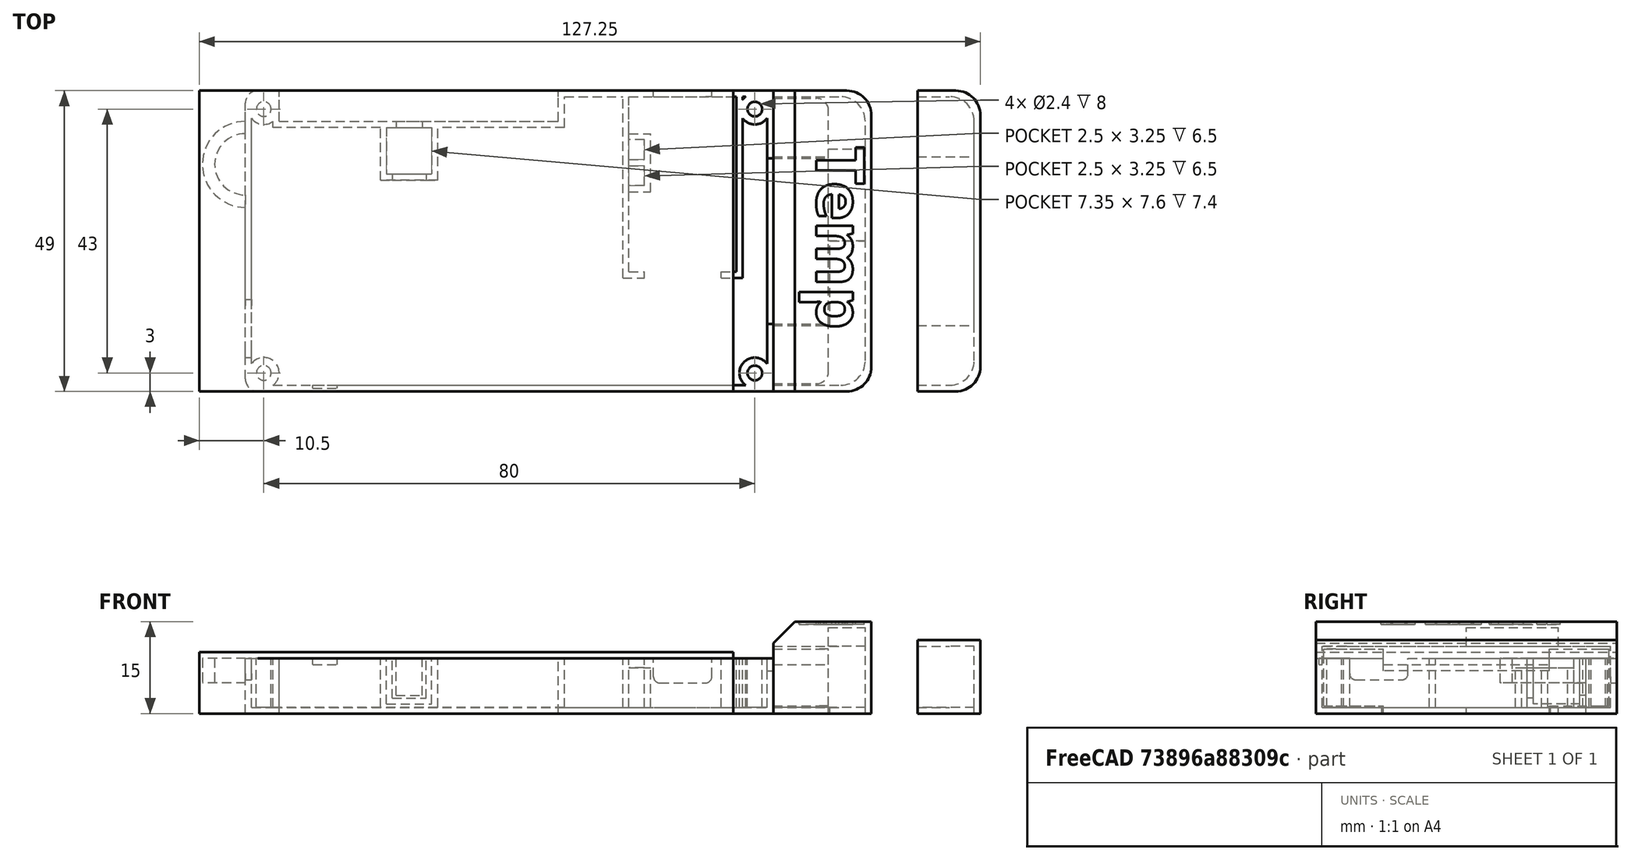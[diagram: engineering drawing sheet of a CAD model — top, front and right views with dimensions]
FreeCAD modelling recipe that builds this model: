
FCSTD DOCUMENT  (FreeCAD 0.20R29410 (Git))
Label: badger2040_case
License: All rights reserved
LicenseURL: http://en.wikipedia.org/wiki/All_rights_reserved
objects: Part::Box×30, Part::MultiFuse×11, Part::Cylinder×10, Part::Cut×10, Part::Fillet×9, Part::Part2DObjectPython×1, Part::Extrusion×1, Part::Chamfer×1
note: 73 computed .brp shape members not serialized (recipe doc carries the construction recipe); baked Part::Feature solids carry a one-line shape summary decoded from their .brp

FEATURE [Part::Box] Box  label="Cube(outer)"
  AttacherType = Attacher::AttachEngine3D
  Height = 9
  Length = 86
  Placement = pos=(0.5,0,-1) rot=(0,0,1;0rad)
  Width = 49
FEATURE [Part::Box] Box001  label="Cube001(connector_cutter)"
  AttacherType = Attacher::AttachEngine3D
  Height = 2
  Length = 10
  Placement = pos=(85.5,11,6) rot=(0,0,1;0rad)
  Width = 27
FEATURE [Part::Cylinder] Cylinder  label="Cylinder(top_left_thread)"
  Angle = 360
  AttacherType = Attacher::AttachEngine3D
  FirstAngle = 0
  Height = 10
  Placement = pos=(3.5,3,0) rot=(0,0,1;0rad)
  Radius = 1.2
  SecondAngle = 0
FEATURE [Part::Cylinder] Cylinder001  label="Cylinder001(top_right_thread)"
  Angle = 360
  AttacherType = Attacher::AttachEngine3D
  FirstAngle = 0
  Height = 10
  Placement = pos=(83.5,3,0) rot=(0,0,1;0rad)
  Radius = 1.2
  SecondAngle = 0
FEATURE [Part::Cylinder] Cylinder002  label="Cylinder002(bottom_left_thread)"
  Angle = 360
  AttacherType = Attacher::AttachEngine3D
  FirstAngle = 0
  Height = 10
  Placement = pos=(3.5,46,0) rot=(0,0,1;0rad)
  Radius = 1.2
  SecondAngle = 0
FEATURE [Part::Cylinder] Cylinder003  label="Cylinder003(bottom_right_thread)"
  Angle = 360
  AttacherType = Attacher::AttachEngine3D
  FirstAngle = 0
  Height = 10
  Placement = pos=(83.5,46,0) rot=(0,0,1;0rad)
  Radius = 1.2
  SecondAngle = 0
FEATURE [Part::Box] Box002  label="Cube(usb_c_charging)"
  AttacherType = Attacher::AttachEngine3D
  Height = 4
  Length = 9.5
  Placement = pos=(67,48,4) rot=(0,0,1;0rad)
  Width = 1
FEATURE [Part::Box] Box003  label="Cube(inner"
  AttacherType = Attacher::AttachEngine3D
  Height = 8
  Length = 84
  Placement = pos=(1.5,1,0) rot=(0,0,1;0rad)
  Width = 47
FEATURE [Part::Box] Box004  label="Cube(button_cutter)"
  AttacherType = Attacher::AttachEngine3D
  Height = 9
  Length = 45.5
  Placement = pos=(6,44,-1) rot=(0,0,1;0rad)
  Width = 5
FEATURE [Part::Box] Box005  label="Cube(button_cutter_wall)"
  AttacherType = Attacher::AttachEngine3D
  Height = 9
  Length = 47.5
  Placement = pos=(5,43,-1) rot=(0,0,1;0rad)
  Width = 6
FEATURE [Part::Box] Box006  label="Cube(usb_c_upload)"
  AttacherType = Attacher::AttachEngine3D
  Height = 3.5
  Length = 1
  Placement = pos=(0.5,5.5,4.5) rot=(0,0,1;0rad)
  Width = 9.5
FEATURE [Part::Cylinder] Cylinder004  label="Cylinder003(bottom_right_outer)"
  Angle = 360
  AttacherType = Attacher::AttachEngine3D
  FirstAngle = 0
  Height = 9
  Placement = pos=(83.5,46,-1) rot=(0,0,1;0rad)
  Radius = 2.5
  SecondAngle = 0
FEATURE [Part::Cylinder] Cylinder005  label="Cylinder(top_left_outer)"
  Angle = 360
  AttacherType = Attacher::AttachEngine3D
  FirstAngle = 0
  Height = 9
  Placement = pos=(3.5,3,-1) rot=(0,0,1;0rad)
  Radius = 2.5
  SecondAngle = 0
FEATURE [Part::Cylinder] Cylinder006  label="Cylinder001(top_right_outer)"
  Angle = 360
  AttacherType = Attacher::AttachEngine3D
  FirstAngle = 0
  Height = 9
  Placement = pos=(83.5,3,-1) rot=(0,0,1;0rad)
  Radius = 2.5
  SecondAngle = 0
FEATURE [Part::Cylinder] Cylinder007  label="Cylinder002(bottom_left_outer)"
  Angle = 360
  AttacherType = Attacher::AttachEngine3D
  FirstAngle = 0
  Height = 9
  Placement = pos=(3.5,46,-1) rot=(0,0,1;0rad)
  Radius = 2.5
  SecondAngle = 0
FEATURE [Part::Fillet] Fillet001
  Base = -> Box003
  Edges = 4 edges r=2: [Edge1,Edge3,Edge5,Edge7]
FEATURE [Part::Fillet] Fillet002
  Base = -> Box006
  Edges = 2 edges r=1: [Edge9,Edge11]
FEATURE [Part::Fillet] Fillet003
  Base = -> Box002
  Edges = 2 edges r=1: [Edge4,Edge8]
FEATURE [Part::MultiFuse] Fusion001
  Shapes = -> [Box001,Cylinder,Cylinder001,Cylinder002,Cylinder003,Box004,Fillet002,Fillet003]
FEATURE [Part::Cylinder] Cylinder017  label="Cylinder017(clip_inner)"
  Angle = 180
  AttacherType = Attacher::AttachEngine3D
  FirstAngle = 0
  Height = 4
  Placement = pos=(-25.5,37,3) rot=(0,0,1;1.5708rad)
  Radius = 5
  SecondAngle = 0
FEATURE [Part::Cylinder] Cylinder016  label="Cylinder(clip_outer)"
  Angle = 180
  AttacherType = Attacher::AttachEngine3D
  FirstAngle = 0
  Height = 4
  Placement = pos=(-25.5,37,3) rot=(0,0,1;1.5708rad)
  Radius = 7
  SecondAngle = 0
FEATURE [Part::Cut] Cut014  label="Cut014(clip)"
  Base = -> Cylinder016
  Placement = pos=(26,0,1) rot=(0,0,1;0rad)
  Tool = -> Cylinder017
FEATURE [Part::Box] Box089  label="Cube009(button_holder)"
  AttacherType = Attacher::AttachEngine3D
  Height = 7.4
  Length = 7.6
  Placement = pos=(-24.5,3,1.6) rot=(0,0,1;0rad)
  Width = 7.35
FEATURE [Part::Box] Box090  label="Cube009(button_holder_hole_top)"
  AttacherType = Attacher::AttachEngine3D
  Height = 6
  Length = 1
  Placement = pos=(-25.5,4.55,3) rot=(0,0,1;0rad)
  Width = 4.25
FEATURE [Part::Box] Box091  label="Cube009(button_holder_hole_bottom)"
  AttacherType = Attacher::AttachEngine3D
  Height = 6.5
  Length = 1
  Placement = pos=(-16.9,3.925,2.5) rot=(0,0,1;0rad)
  Width = 5.5
FEATURE [Part::MultiFuse] Fusion002  label="Fusion002(button)"
  Placement = pos=(20.5,18.5,-1) rot=(0,0,-1;1.5708rad)
  Shapes = -> [Box089,Box090,Box091]
FEATURE [Part::Box] Box092  label="Cube(button_outer)"
  AttacherType = Attacher::AttachEngine3D
  Height = 9
  Length = 9.35
  Placement = pos=(22.5,34.4,-1) rot=(0,0,1;0rad)
  Width = 8.6
FEATURE [Part::Box] Box093  label="Cube(charger_inner)"
  AttacherType = Attacher::AttachEngine3D
  Height = 8
  Length = 17.5
  Placement = pos=(63,19.5,0) rot=(0,0,1;0rad)
  Width = 28.5
FEATURE [Part::Box] Box094  label="Cube(charger_outer)"
  AttacherType = Attacher::AttachEngine3D
  Height = 8
  Length = 19.5
  Placement = pos=(62,18.5,0) rot=(0,0,1;0rad)
  Width = 29.5
FEATURE [Part::Box] Box095  label="Cube(charger_wire_cutter)"
  AttacherType = Attacher::AttachEngine3D
  Height = 8
  Length = 12.5
  Placement = pos=(65.5,18.5,0) rot=(0,0,1;0rad)
  Width = 1
FEATURE [Part::Box] Box096  label="Cube(charger_led_light_pipe_inner)"
  AttacherType = Attacher::AttachEngine3D
  Height = 8.5
  Length = 2.5
  Placement = pos=(63,33.5,-0.5) rot=(0,0,1;0rad)
  Width = 7.5
FEATURE [Part::Box] Box097  label="Cube(charger_led_light_pipe_outer)"
  AttacherType = Attacher::AttachEngine3D
  Height = 6.5
  Length = 3.5
  Placement = pos=(63,32.5,0) rot=(0,0,1;0rad)
  Width = 9.5
FEATURE [Part::Box] Box098  label="Cube(charger_led_light_pipe_divide)"
  AttacherType = Attacher::AttachEngine3D
  Height = 6.5
  Length = 2.5
  Placement = pos=(63,36.75,0) rot=(0,0,1;0rad)
  Width = 1
FEATURE [Part::Box] Box099  label="Cube(act_led_cutter)"
  AttacherType = Attacher::AttachEngine3D
  Height = 1
  Length = 4
  Placement = pos=(11.5,0.5,7) rot=(0,0,1;0rad)
  Width = 0.5
FEATURE [Part::MultiFuse] Fusion004
  Shapes = -> [Fusion002,Box093,Box095,Box099]
FEATURE [Part::Box] Box100  label="Cube(connector_support)"
  AttacherType = Attacher::AttachEngine3D
  Height = 10.5
  Length = 9
  Placement = pos=(86.5,1.25,-1) rot=(0,0,1;0rad)
  Width = 46.5
FEATURE [Part::Fillet] Fillet
  Base = -> Box
  Edges = 2 edges r=2: [Edge1,Edge3]
FEATURE [Part::Cut] Cut
  Base = -> Fillet
  Tool = -> Fillet001
FEATURE [Part::MultiFuse] Fusion
  Shapes = -> [Cut,Box005,Box092]
FEATURE [Part::MultiFuse] Fusion005
  Shapes = -> [Cylinder007,Cylinder006,Cylinder005,Cylinder004,Fusion]
FEATURE [Part::Box] Box101  label="Cube001(connector_cutter)001"
  AttacherType = Attacher::AttachEngine3D
  Height = 2.5
  Length = 10
  Placement = pos=(85.5,11,7) rot=(0,0,1;0rad)
  Width = 27
FEATURE [Part::Cut] Cut015
  Base = -> Fusion005
  Tool = -> Fusion001
FEATURE [Part::MultiFuse] Fusion006
  Shapes = -> [Cut015,Box094]
FEATURE [Part::Cut] Cut016
  Base = -> Fusion006
  Tool = -> Fusion004
FEATURE [Part::Cut] Cut017
  Base = -> Box097
  Tool = -> Box096
FEATURE [Part::MultiFuse] Fusion007
  Shapes = -> [Cut017,Cut016,Box098,Cut014]
FEATURE [Part::Fillet] Fillet004
  Base = -> Box100
  Edges = 2 edges r=2: [Edge5,Edge7]
FEATURE [Part::Cut] Cut018
  Base = -> Fillet004
  Tool = -> Box101
FEATURE [Part::Box] Box102  label="Cube(test_cutter)"
  AttacherType = Attacher::AttachEngine3D
  Height = 10
  Length = 87
  Placement = pos=(-7,0,-1) rot=(0,0,1;0rad)
  Width = 49
FEATURE [Part::MultiFuse] Fusion008
  Shapes = -> [Cut018,Fusion007]
FEATURE [Part::Box] Box103  label="Cube001(sensor_cover_inner)"
  AttacherType = Attacher::AttachEngine3D
  Height = 10
  Length = 15
  Placement = pos=(86.5,1,0) rot=(0,0,1;0rad)
  Width = 47
FEATURE [Part::Box] Box104  label="Cube001(sensor_cover_inner_middle)"
  AttacherType = Attacher::AttachEngine3D
  Height = 14
  Length = 6
  Placement = pos=(95.5,24.5,-1) rot=(0,0,1;0rad)
  Width = 15
FEATURE [Part::Box] Box105  label="Cube001(sensor_cover_outer)"
  AttacherType = Attacher::AttachEngine3D
  Height = 15
  Length = 16
  Placement = pos=(86.5,0,-1) rot=(0,0,1;0rad)
  Width = 49
FEATURE [Part::Part2DObjectPython] ShapeString  # Draft 2D object (typed FeaturePython)
  FontFile = <userpath>/stuff/3dprinting/fonts/open-sans/OpenSans-Bold.ttf
  MakeFace = true
  Placement = pos=(93.5,40,13.5) rot=(0,0,-1;1.5708rad)
  Size = 10
  String = Temp
  Tracking = 0
FEATURE [Part::Extrusion] Extrude
  Base = -> ShapeString
  Dir = (0,0,1)
  DirMode = 2
  FaceMakerClass = Part::FaceMakerBullseye
  LengthFwd = 0.5
  LengthRev = 0
  Solid = false
  Symmetric = false
FEATURE [Part::Box] Box108  label="Cube001"
  AttacherType = Attacher::AttachEngine3D
  Height = 1.25
  Length = 9
  Placement = pos=(86.5,0,-1) rot=(0,0,1;0rad)
  Width = 11
FEATURE [Part::Box] Box109  label="Cube002"
  AttacherType = Attacher::AttachEngine3D
  Height = 1.25
  Length = 9
  Placement = pos=(86.5,38,-1) rot=(0,0,1;0rad)
  Width = 11
FEATURE [Part::MultiFuse] Fusion010
  Shapes = -> [Box108,Box109]
FEATURE [Part::Cut] Cut021  label="Cut021(case)"
  Base = -> Fusion008
  Tool = -> Fusion010
FEATURE [Part::Box] Box110  label="Cube001(sensor_cover_inner_middle)003"
  AttacherType = Attacher::AttachEngine3D
  Height = 10
  Length = 9.25
  Placement = pos=(86.5,10.75,-1) rot=(0,0,1;0rad)
  Width = 27.5
FEATURE [Part::Fillet] Fillet009
  Base = -> Box105
  Edges = 2 edges r=4: [Edge5,Edge7]
FEATURE [Part::Fillet] Fillet010
  Base = -> Box103
  Edges = 2 edges r=4: [Edge5,Edge7]
FEATURE [Part::MultiFuse] Fusion011
  Shapes = -> [Fillet010,Box110,Box104]
FEATURE [Part::Cut] Cut022
  Base = -> Fillet009
  Tool = -> Fusion011
FEATURE [Part::Chamfer] Chamfer
  Base = -> Cut022
  Edges = 1 edges r=3.5: [Edge6]
FEATURE [Part::Cut] Cut023  label="Cut023(GPIO_temp)"
  Base = -> Chamfer
  Tool = -> Extrude
FEATURE [Part::Box] Box111  label="Cube001(sensor_cover_inner)001"
  AttacherType = Attacher::AttachEngine3D
  Height = 10
  Length = 9.25
  Placement = pos=(110,1,0) rot=(0,0,1;0rad)
  Width = 47
FEATURE [Part::Box] Box113  label="Cube001(sensor_cover_outer)001"
  AttacherType = Attacher::AttachEngine3D
  Height = 12
  Length = 10.25
  Placement = pos=(110,0,-1) rot=(0,0,1;0rad)
  Width = 49
FEATURE [Part::Box] Box114  label="Cube001(sensor_cover_inner_middle)005"
  AttacherType = Attacher::AttachEngine3D
  Height = 10
  Length = 9.25
  Placement = pos=(110,10.75,-1) rot=(0,0,1;0rad)
  Width = 27.5
FEATURE [Part::Fillet] Fillet011
  Base = -> Box113
  Edges = 2 edges r=4: [Edge5,Edge7]
FEATURE [Part::Fillet] Fillet012
  Base = -> Box111
  Edges = 2 edges r=4: [Edge5,Edge7]
FEATURE [Part::MultiFuse] Fusion012
  Shapes = -> [Fillet012,Box114]
FEATURE [Part::Cut] Cut024  label="Cut024(GPIO_cover)"
  Base = -> Fillet011
  Tool = -> Fusion012
